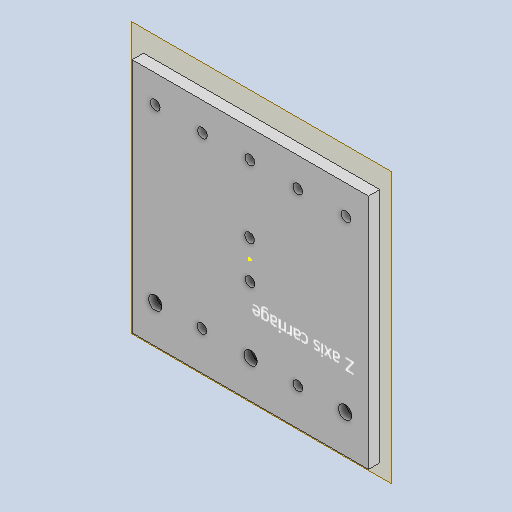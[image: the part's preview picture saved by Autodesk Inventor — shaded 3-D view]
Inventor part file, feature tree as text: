
AUTODESK INVENTOR PART (.ipt)
format: ipt  version: 2023.2 (Build 272271000, 271)  size: 174,592 bytes
history: native  units: mm
features: reference x8, sketch x5, hole x3, other x3, plane x1, extrude x1
ambient origin geometry x8: Origin, YZ Plane, XZ Plane, XY Plane, X Axis, Y Axis, Z Axis, Center Point
bodies: Solid1 (feature_tree)
feature tree (21):
  plane  "Work Plane1"
  extrude  "Extrusion1"  Depth=50.2mm
  hole  "Hole1"  [1 undecoded]
  hole  "Hole2"  [1 undecoded]
  hole  "Hole3"  [1 undecoded]
  sketch  "Sketch5"  dims[d8=7.1mm d9=6.0mm d10=7.5mm d11=2.0mm d12=90.0deg d13=8.0mm d14=20.594885mm d15=5.1mm d16=6.0mm d17=7.5mm d18=2.0mm d19=90.0deg d20=8.0mm d21=20.594885mm d22=5.1mm d23=6.0mm d24=7.5mm d25=2.0mm d26=90.0deg d27=8.0mm d28=20.594885mm]
  sketch  "Sketch1"  dims[d0=100.4mm d1=50.2mm]
  reference  "Reference1"
  reference  "Reference2"
  reference  "Reference3"
  reference  "Reference4"
  reference  "Reference5"
  reference  "Reference6"
  reference  "Reference7"
  reference  "Reference8"
  sketch  "Sketch2"  dims[d2=25.1mm d3=25.1mm]
  sketch  "Sketch3"  dims[d4=10.0mm d5=20.0mm]
  sketch  "Sketch4"  dims[d6=6.0mm d7=0.0mm]
  parser-record x1  (decoder bookkeeping rows leaked as tree rows — omitted from the tree; the rows remain in map.json)
  other  "Main Assembly.iam"
  other  "X axis carriage small:1"
note: 3 required parameter values undecoded (feature->parameter linkage not recoverable at this tier; creation-order binding heuristic only, values carry confidence <= 0.55)
note: 1 file-system path scrubbed to <path> (originals preserved in map.json)
